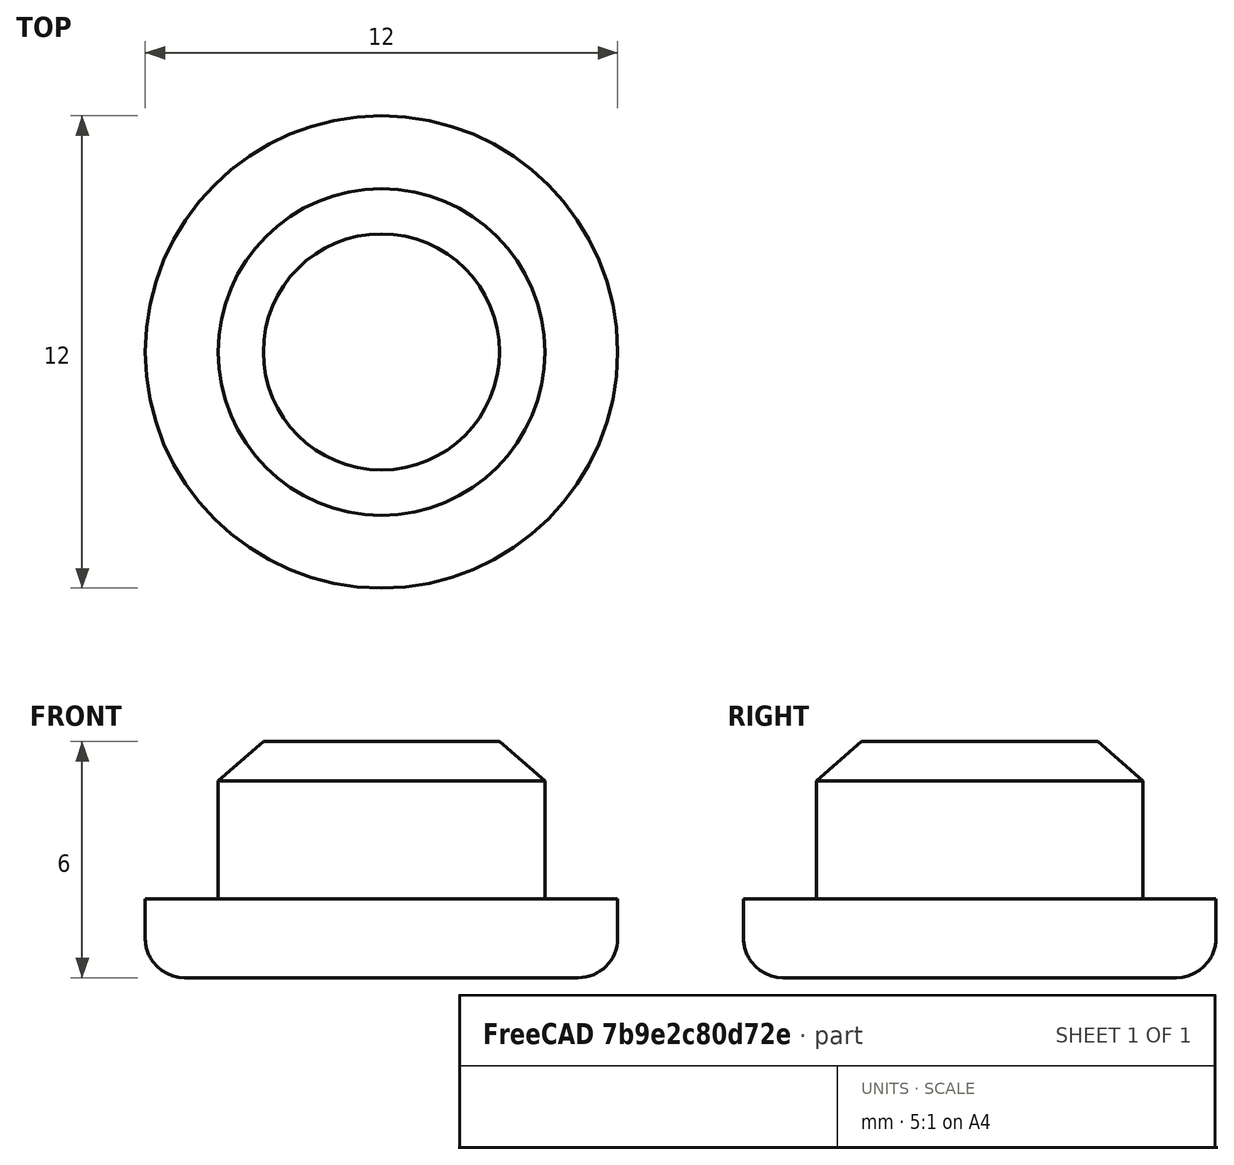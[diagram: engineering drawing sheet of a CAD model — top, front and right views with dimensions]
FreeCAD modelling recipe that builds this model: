
FCSTD DOCUMENT  (FreeCAD 0.18R16131 (Git))
Label: glowstick_stopper
License: All rights reserved
LicenseURL: http://en.wikipedia.org/wiki/All_rights_reserved
objects: Part::Cylinder×2, Part::Cone×1, Part::Fillet×1, Part::MultiFuse×1
note: 5 computed .brp shape members not serialized (recipe doc carries the construction recipe); baked Part::Feature solids carry a one-line shape summary decoded from their .brp

FEATURE [Part::Cylinder] Cylinder
  Angle = 360
  AttacherType = Attacher::AttachEngine3D
  Height = 3
  Radius = 4.15
FEATURE [Part::Cone] Cone
  Angle = 360
  AttacherType = Attacher::AttachEngine3D
  Height = 1
  Placement = pos=(0,0,3) rot=(0,0,1;0rad)
  Radius1 = 4.15
  Radius2 = 3
FEATURE [Part::Cylinder] Cylinder001
  Angle = 360
  AttacherType = Attacher::AttachEngine3D
  Height = 2
  Placement = pos=(0,0,-2) rot=(0,0,1;0rad)
  Radius = 6
FEATURE [Part::Fillet] Fillet
  Base = -> Cylinder001
  Edges = 1 edges r=1: [Edge3]
FEATURE [Part::MultiFuse] Fusion
  Shapes = -> [Fillet,Cylinder,Cone]
